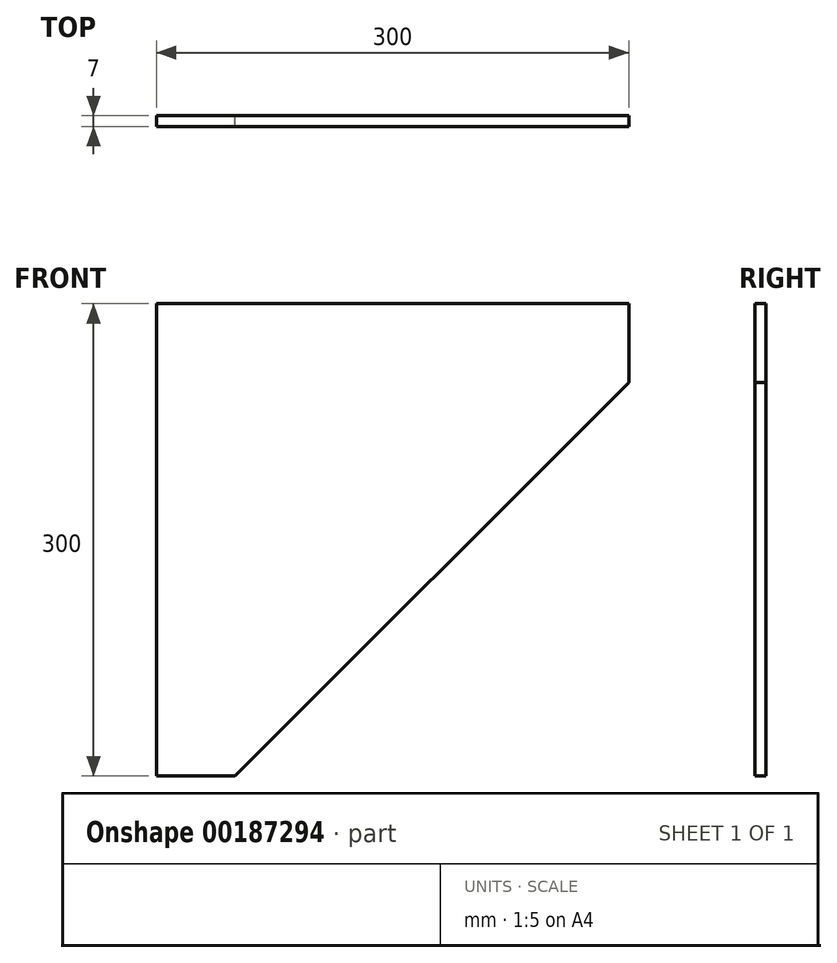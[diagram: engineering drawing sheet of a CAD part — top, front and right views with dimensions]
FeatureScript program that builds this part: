
annotation { "Feature Type Name" : "Feature", "Feature Type Description" : "" }
export const myFeature = defineFeature(function(context is Context, id is Id, definition is map)
    precondition{}
    {
        {
            var Q0;
            Q0=qCreatedBy(makeId("Front.planeOp"),FACE);
            var sketch = newSketch(context, id + "F0", { "sketchPlane" : qUnion([Q0])});
            skLineSegment(sketch, "E0.bottom", {"start": v(0, 0) * mm, "end": v(50, 0) * mm});
            skLineSegment(sketch, "E0.top", {"start": v(0, 300) * mm, "end": v(300, 300) * mm});
            skLineSegment(sketch, "E0.left", {"start": v(0, 0) * mm, "end": v(0, 300) * mm});
            skLineSegment(sketch, "E0.right", {"start": v(300, 250) * mm, "end": v(300, 300) * mm});
            skLineSegment(sketch, "E1", {"start": v(50, 0) * mm, "end": v(300, 250) * mm});
            skSolve(sketch);
        }
        {
            var Q0;
            Q0=makeQuery(id+"F0.imprint","IMPRINT",FACE,{"disambiguationData":[TD([[makeQuery(id+"F0.imprint","IMPRINT",EDGE,{"derivedFrom":sQuery(id+"F0.wireOp",EDGE,"E0.bottom")}),1.0]])]});
            extrude(context, id + "F1", {"entities" : qUnion([Q0]), "depth" : 7 * mm});
        }
    });
